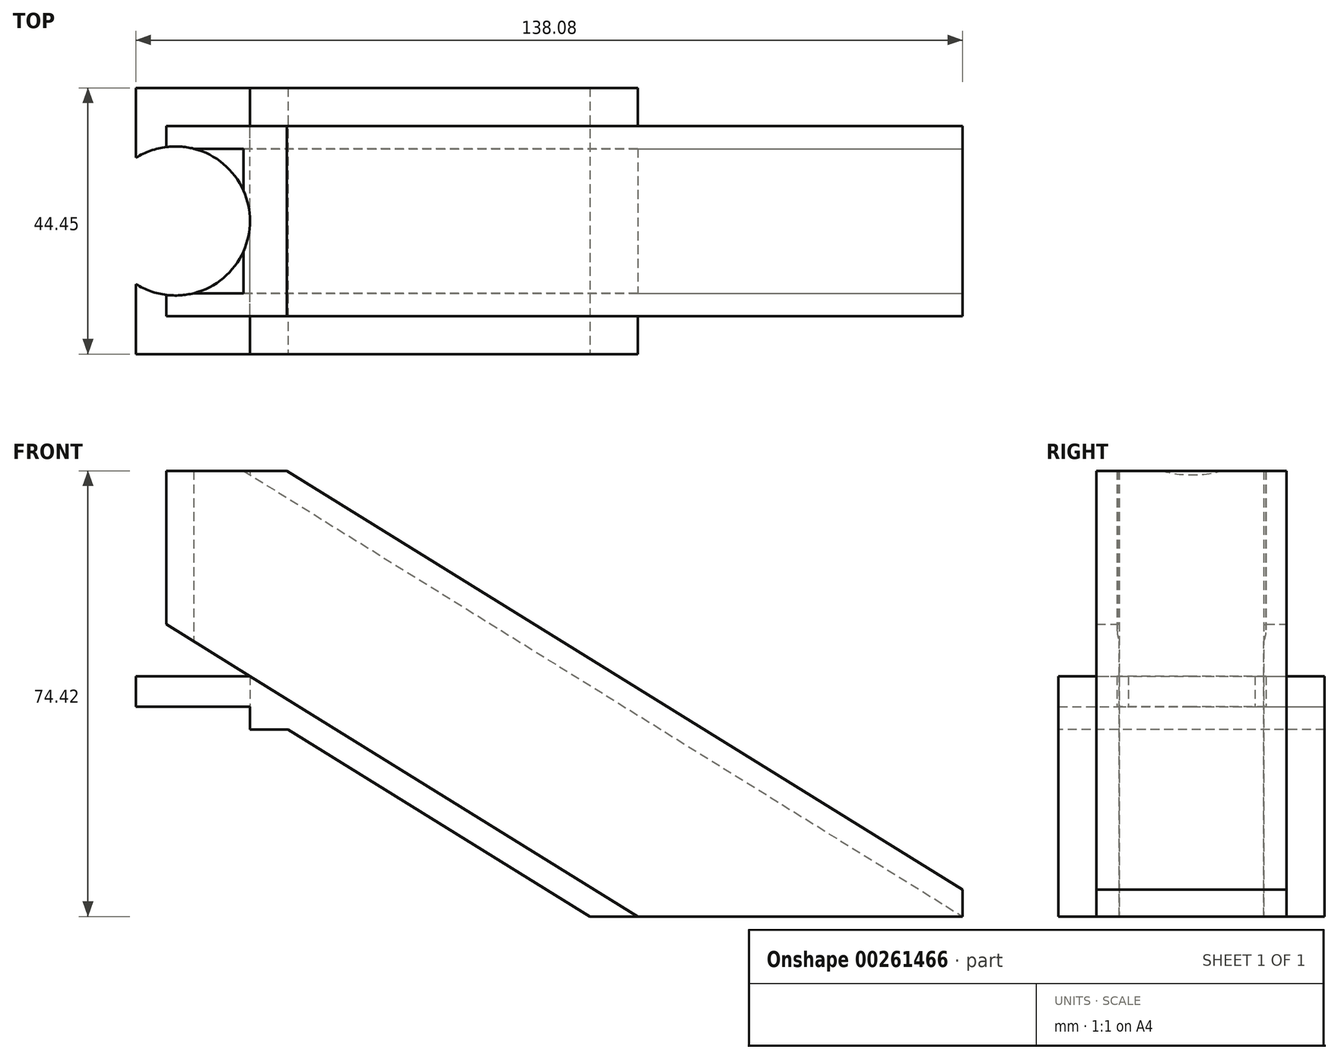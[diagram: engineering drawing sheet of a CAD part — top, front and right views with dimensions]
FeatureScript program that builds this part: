
annotation { "Feature Type Name" : "Feature", "Feature Type Description" : "" }
export const myFeature = defineFeature(function(context is Context, id is Id, definition is map)
    precondition{}
    {
        {
            var Q0;
            Q0=qCreatedBy(makeId("Front.planeOp"),FACE);
            var sketch = newSketch(context, id + "F0", { "sketchPlane" : qUnion([Q0])});
            skLineSegment(sketch, "E0", {"start": v(-19.05, 0) * mm, "end": v(0, 0) * mm});
            skLineSegment(sketch, "E1", {"start": v(0, 0) * mm, "end": v(0, -35.05) * mm});
            skLineSegment(sketch, "E2", {"start": v(0, -35.05) * mm, "end": v(64.77, -35.05) * mm});
            skLineSegment(sketch, "E3", {"start": v(64.77, -35.05) * mm, "end": v(0, 5.08) * mm});
            skLineSegment(sketch, "E4", {"start": v(0, 5.08) * mm, "end": v(-19.05, 5.08) * mm});
            skLineSegment(sketch, "E5", {"start": v(-19.05, 5.08) * mm, "end": v(-19.05, 0) * mm});
            skSolve(sketch);
        }
        {
            var Q0;
            Q0 = qSketchRegion(id + "F0", true);
            extrude(context, id + "F1", {"entities" : qUnion([Q0]), "depth" : 34.3 * mm, "offsetDistance" : 25.4 * mm, "hasSecondDirection" : true, "secondDirectionOppositeDirection" : true, "secondDirectionDepth" : 10.16 * mm});
        }
        {
            var Q0;
            Q0=qCreatedBy(makeId("Front.planeOp"),FACE);
            var sketch = newSketch(context, id + "F2", { "sketchPlane" : qUnion([Q0])});
            skLineSegment(sketch, "E6", {"start": v(-13.97, 13.74) * mm, "end": v(64.77, -35.05) * mm});
            skLineSegment(sketch, "E7", {"start": v(64.77, -35.05) * mm, "end": v(126.26, -35.05) * mm});
            skLineSegment(sketch, "E8", {"start": v(126.26, -35.05) * mm, "end": v(-13.97, 51.84) * mm});
            skLineSegment(sketch, "E9", {"start": v(-13.97, 51.84) * mm, "end": v(-13.97, 13.74) * mm});
            skSolve(sketch);
        }
        {
            var Q0;
            Q0 = qSketchRegion(id + "F2", true);
            extrude(context, id + "F3", {"entities" : qUnion([Q0]), "operationType" : NewBodyOperationType.ADD, "depth" : 27.94 * mm, "offsetDistance" : 25.4 * mm, "hasSecondDirection" : true, "secondDirectionOppositeDirection" : true, "secondDirectionDepth" : 3.8 * mm});
        }
        {
            var Q0;
            Q0=makeQuery(id+"F1.opExtrude","SWEPT_FACE",FACE,{"disambiguationData":[OSD([sQuery(id+"F0.wireOp",EDGE,"E0")])]});
            var sketch = newSketch(context, id + "F4", { "sketchPlane" : qUnion([Q0])});
            skCircle(sketch, "E10", {"center": v(-12.45, 12.07) * mm, "radius": 12.45 * mm});
            skSolve(sketch);
        }
        {
            var Q0;
            Q0 = qSketchRegion(id + "F4", true);
            extrude(context, id + "F5", {"entities" : qUnion([Q0]), "operationType" : NewBodyOperationType.REMOVE, "oppositeDirection" : true, "depth" : 39.37 * mm, "offsetDistance" : 25.4 * mm});
        }
        {
            var Q0;
            Q0=makeQuery(id+"F5.boolean.opBoolean","COPY",FACE,{"derivedFrom":makeQuery(id+"F5.opExtrude","CAP_FACE",FACE,{"disambiguationData":[OSD([sQuery(id+"F4.wireOp",EDGE,"E10")])],"isStart":false})});
            var sketch = newSketch(context, id + "F6", { "sketchPlane" : qUnion([Q0])});
            skLineSegment(sketch, "E11.bottom", {"start": v(-37.07, 41.92) * mm, "end": v(15.88, 41.92) * mm});
            skLineSegment(sketch, "E11.top", {"start": v(-37.07, -21.45) * mm, "end": v(15.88, -21.45) * mm});
            skLineSegment(sketch, "E11.left", {"start": v(-37.07, 41.92) * mm, "end": v(-37.07, -21.45) * mm});
            skLineSegment(sketch, "E11.right", {"start": v(15.88, 41.92) * mm, "end": v(15.88, -21.45) * mm});
            skSolve(sketch);
        }
        {
            var Q0;
            Q0 = qSketchRegion(id + "F6", true);
            extrude(context, id + "F7", {"entities" : qUnion([Q0]), "operationType" : NewBodyOperationType.REMOVE, "oppositeDirection" : true, "depth" : 25.4 * mm, "offsetDistance" : 25.4 * mm});
        }
        {
            var Q0;
            Q0=qCreatedBy(makeId("Front.planeOp"),FACE);
            var sketch = newSketch(context, id + "F8", { "sketchPlane" : qUnion([Q0])});
            skLineSegment(sketch, "E12", {"start": v(-10.16, 45) * mm, "end": v(154.41, -56.98) * mm});
            skLineSegment(sketch, "E13", {"start": v(154.41, -56.98) * mm, "end": v(100.16, -56.98) * mm});
            skLineSegment(sketch, "E14", {"start": v(100.16, -56.98) * mm, "end": v(-10.16, 11.38) * mm});
            skLineSegment(sketch, "E15", {"start": v(-10.16, 11.38) * mm, "end": v(-10.16, 45) * mm});
            skSolve(sketch);
        }
        {
            var Q0;
            Q0 = qSketchRegion(id + "F8", true);
            extrude(context, id + "F9", {"entities" : qUnion([Q0]), "operationType" : NewBodyOperationType.REMOVE, "depth" : 24.13 * mm, "offsetDistance" : 25.4 * mm});
        }
        {
            var Q0;
            Q0=makeQuery(id+"F1.opExtrude","CAP_FACE",FACE,{"disambiguationData":[OSD([sQuery(id+"F0.wireOp",EDGE,"E0"),sQuery(id+"F0.wireOp",EDGE,"E1"),sQuery(id+"F0.wireOp",EDGE,"E2"),sQuery(id+"F0.wireOp",EDGE,"E3"),sQuery(id+"F0.wireOp",EDGE,"E4"),sQuery(id+"F0.wireOp",EDGE,"E5")])],"isStart":false});
            var sketch = newSketch(context, id + "F10", { "sketchPlane" : qUnion([Q0])});
            skLineSegment(sketch, "E16", {"start": v(0, -35.05) * mm, "end": v(0, -3.81) * mm});
            skLineSegment(sketch, "E17", {"start": v(0, -3.81) * mm, "end": v(6.35, -3.81) * mm});
            skLineSegment(sketch, "E18", {"start": v(6.35, -3.8) * mm, "end": v(56.77, -35.05) * mm});
            skLineSegment(sketch, "E19", {"start": v(56.77, -35.05) * mm, "end": v(0, -35.05) * mm});
            skSolve(sketch);
        }
        {
            var Q0;
            Q0 = qSketchRegion(id + "F10", true);
            extrude(context, id + "F11", {"entities" : qUnion([Q0]), "operationType" : NewBodyOperationType.REMOVE, "oppositeDirection" : true, "depth" : 50.8 * mm, "offsetDistance" : 25.4 * mm});
        }
        {
            var Q0;
            Q0=makeQuery(id+"F3.boolean.opBoolean","MERGE",FACE,{"derivedFrom":[makeQuery(id+"F1.opExtrude","SWEPT_FACE",FACE,{"disambiguationData":[OSD([sQuery(id+"F0.wireOp",EDGE,"E2")])]}),makeQuery(id+"F3.opExtrude","SWEPT_FACE",FACE,{"disambiguationData":[OSD([sQuery(id+"F2.wireOp",EDGE,"E7")])]})]});
            var sketch = newSketch(context, id + "F12", { "sketchPlane" : qUnion([Q0])});
            skLineSegment(sketch, "E20.bottom", {"start": v(126.26, -3.81) * mm, "end": v(119.03, -3.81) * mm});
            skLineSegment(sketch, "E20.top", {"start": v(126.26, 27.94) * mm, "end": v(119.03, 27.94) * mm});
            skLineSegment(sketch, "E20.left", {"start": v(126.26, -3.81) * mm, "end": v(126.26, 27.94) * mm});
            skLineSegment(sketch, "E20.right", {"start": v(119.03, -3.81) * mm, "end": v(119.03, 27.94) * mm});
            skSolve(sketch);
        }
        {
            var Q0;
            Q0 = qSketchRegion(id + "F12", true);
            extrude(context, id + "F13", {"entities" : qUnion([Q0]), "operationType" : NewBodyOperationType.REMOVE, "oppositeDirection" : true, "depth" : 25.4 * mm, "offsetDistance" : 25.4 * mm});
        }
    });
